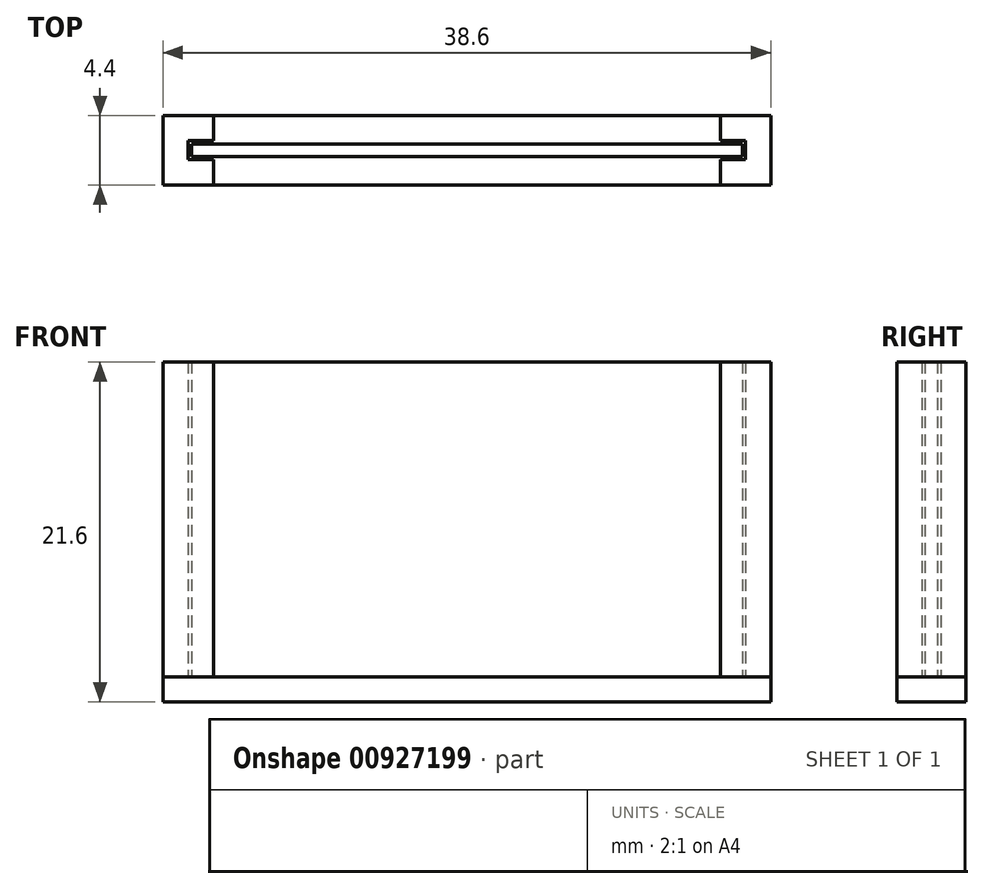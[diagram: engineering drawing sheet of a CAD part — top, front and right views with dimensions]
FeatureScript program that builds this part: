
annotation { "Feature Type Name" : "Feature", "Feature Type Description" : "" }
export const myFeature = defineFeature(function(context is Context, id is Id, definition is map)
    precondition{}
    {
        {
            assignVariable(context, id + "F0", {"name" : "depth", "anyValue" : .8});
        }
        {
            var Q0;
            Q0=qCreatedBy(makeId("Top.planeOp"),FACE);
            var sketch = newSketch(context, id + "F1", { "sketchPlane" : qUnion([Q0])});
            skLineSegment(sketch, "E0.bottom", {"start": v(-17.5, 0.4) * mm, "end": v(17.5, 0.4) * mm});
            skLineSegment(sketch, "E0.top", {"start": v(-17.5, -0.4) * mm, "end": v(17.5, -0.4) * mm});
            skLineSegment(sketch, "E0.left", {"start": v(-17.5, 0.4) * mm, "end": v(-17.5, -0.4) * mm});
            skLineSegment(sketch, "E0.right", {"start": v(17.5, 0.4) * mm, "end": v(17.5, -0.4) * mm});
            skPoint(sketch, "E0.middle", {"position": v(0, 0) * mm});
            skLineSegment(sketch, "E1.0", {"start": v(-17.7, 0.6) * mm, "end": v(17.7, 0.6) * mm});
            skLineSegment(sketch, "E1.1", {"start": v(-17.7, 0.6) * mm, "end": v(-17.7, -0.6) * mm});
            skLineSegment(sketch, "E1.2", {"start": v(-17.7, -0.6) * mm, "end": v(17.7, -0.6) * mm});
            skLineSegment(sketch, "E1.3", {"start": v(17.7, 0.6) * mm, "end": v(17.7, -0.6) * mm});
            skLineSegment(sketch, "E2.0", {"start": v(-19.3, -2.2) * mm, "end": v(19.3, -2.2) * mm});
            skLineSegment(sketch, "E2.1", {"start": v(-19.3, 2.2) * mm, "end": v(-19.3, -2.2) * mm});
            skLineSegment(sketch, "E2.2", {"start": v(-19.3, 2.2) * mm, "end": v(19.3, 2.2) * mm});
            skLineSegment(sketch, "E2.3", {"start": v(19.3, 2.2) * mm, "end": v(19.3, -2.2) * mm});
            skLineSegment(sketch, "E3", {"start": v(-16.1, 0.6) * mm, "end": v(-16.1, 2.2) * mm});
            skLineSegment(sketch, "E4", {"start": v(-16.1, -0.6) * mm, "end": v(-16.1, -2.2) * mm});
            skLineSegment(sketch, "E5", {"start": v(16.1, 0.6) * mm, "end": v(16.1, 2.2) * mm});
            skLineSegment(sketch, "E6", {"start": v(16.1, -0.6) * mm, "end": v(16.1, -2.2) * mm});
            skSolve(sketch);
        }
        {
            var Q0;
            {var subQ1=sQuery(id+"F1.wireOp",EDGE,"E1.1");Q0=makeQuery(id+"F1.imprint","IMPRINT",FACE,{"disambiguationData":[TD([[makeQuery(id+"F1.imprint","IMPRINT",EDGE,{"derivedFrom":subQ1}),-1.0]])]});}
            var Q1;
            {var subQ3=sQuery(id+"F1.wireOp",EDGE,"E1.3");Q1=makeQuery(id+"F1.imprint","IMPRINT",FACE,{"disambiguationData":[TD([[makeQuery(id+"F1.imprint","IMPRINT",EDGE,{"derivedFrom":subQ3}),1.0]])]});}
            extrude(context, id + "F2", {"entities" : qUnion([Q0, Q1]), "depth" : 20 * mm, "offsetDistance" : 25 * mm});
        }
        {
            var Q0;
            Q0=makeQuery(id+"F1.imprint","IMPRINT",FACE,{"disambiguationData":[TD([[makeQuery(id+"F1.imprint","IMPRINT",EDGE,{"derivedFrom":sQuery(id+"F1.wireOp",EDGE,"E0.bottom")}),1.0]])]});
            var Q1;
            Q1=makeQuery(id+"F1.imprint","IMPRINT",FACE,{"disambiguationData":[TD([[makeQuery(id+"F1.imprint","IMPRINT",EDGE,{"derivedFrom":sQuery(id+"F1.wireOp",EDGE,"E0.bottom")}),-1.0]])]});
            var Q2;
            {var subQ0=sQuery(id+"F1.wireOp",EDGE,"E3");Q2=makeQuery(id+"F1.imprint","IMPRINT",FACE,{"disambiguationData":[TD([[makeQuery(id+"F1.imprint","IMPRINT",EDGE,{"derivedFrom":subQ0}),-1.0]])]});}
            var Q3;
            {var subQ0=sQuery(id+"F1.wireOp",EDGE,"E4");Q3=makeQuery(id+"F1.imprint","IMPRINT",FACE,{"disambiguationData":[TD([[makeQuery(id+"F1.imprint","IMPRINT",EDGE,{"derivedFrom":subQ0}),1.0]])]});}
            var Q4;
            {var subQ1=sQuery(id+"F1.wireOp",EDGE,"E1.1");Q4=makeQuery(id+"F1.imprint","IMPRINT",FACE,{"disambiguationData":[TD([[makeQuery(id+"F1.imprint","IMPRINT",EDGE,{"derivedFrom":subQ1}),-1.0]])]});}
            var Q5;
            {var subQ3=sQuery(id+"F1.wireOp",EDGE,"E1.3");Q5=makeQuery(id+"F1.imprint","IMPRINT",FACE,{"disambiguationData":[TD([[makeQuery(id+"F1.imprint","IMPRINT",EDGE,{"derivedFrom":subQ3}),1.0]])]});}
            extrude(context, id + "F3", {"entities" : qUnion([Q0, Q1, Q2, Q3, Q4, Q5]), "oppositeDirection" : true, "depth" : (getVariable(context, 'depth') * 2) * mm, "offsetDistance" : 25 * mm});
        }
        {
            var Q0;
            Q0=makeQuery(id+"F1.imprint","IMPRINT",FACE,{"disambiguationData":[TD([[makeQuery(id+"F1.imprint","IMPRINT",EDGE,{"derivedFrom":sQuery(id+"F1.wireOp",EDGE,"E0.bottom")}),-1.0]])]});
            extrude(context, id + "F4", {"entities" : qUnion([Q0]), "depth" : 20 * mm, "offsetDistance" : 25 * mm});
        }
    });
